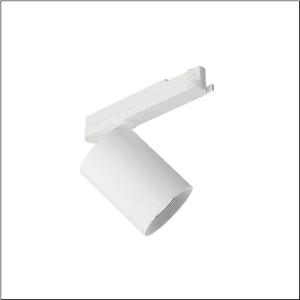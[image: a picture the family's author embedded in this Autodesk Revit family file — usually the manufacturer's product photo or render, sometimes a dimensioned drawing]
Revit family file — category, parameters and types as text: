
# Revit family: spot_21_51se12mbb5b
name_source: partatom
category: Lighting Fixtures
units: mm (PartAtom-declared; Revit-internal decimal feet)

## family parameters
Cut with Voids When Loaded = No
Host = Face
Light Source = No
Part Type = Normal
Room Calculation Point = No
Round Connector Dimension = Use Diameter
Shared = No

## types (1)
- --- (1 x LED, 5300 lm, 41.7 W, 3000K)
    Apparent Load = 42 VA
    CIE Flux Codes = 95 98 99 100 100
    Color Rendering = 90
    Color Temperature = 3000K
    Default Elevation = 1800 mm
    Description = Spot 21, directional spotlight, light control with lens, of PMMA, LED rated luminous flux: 5.100lm, light colour: 930, control gear: ECG Multilumen, with 3-phase adapter, mains connection: 220..240V, AC, 50/60Hz, of aluminium, traffic white (RAL 9016), length: 213mm, diameter: 105mm, protection rating (complete): IP20, insulation class (complete): insulation class I (protective earthing), certification: CE, impact resistance: IK02, permissible ambient temperature for indoor applications: -20..+40°C, packaging unit: 1 piece
    Height = 175 mm
    Lamp = 1 x LED
    Lamp Light Flux = 5300 lm
    Lamp Power = 41.7 W
    Lamp count = 1
    Length = 105 mm
    Luminous efficacy = 127 lm/W
    Manufacturer = Siteco
    ModVariant = No
    Model = 51SE12MBB5B
    Mounting Place = Ceiling
    Mounting Type = Pendant
    Number of Poles = 1
    OnlyDefault = Yes
    Power Factor = 1
    Product Name = Spot 21
    Product group = directional spotlight
    ProductGroupID = 905
    Protection Class = Protection class I
    Protection Degree = IP 20
    RLX_Detail_Level = 1
    RLX_Emergency_Light_Flux = 0 lm
    RLX_Emergency_Type = 0
    RLX_Emergency_Type_DB = No
    RlxData = <blob elided: 17649 chars, md5=ee2d00f4>
    Socket = socket
    Standby Power = 0 W
    System Light Flux = 5300 lm
    System Power = 42 W
    Type Comments = factory setting: luminous flux: 100 % | (ON | ON | ON | ON) | 1050 mA
    Type Image = l_1003976.jpg
    URL = http://relux.com
    VarID = @adj_114243
    Voltage = 0 V
    Weight = 0.00 kg
    Width = 0 mm  [stored 0 ft]

note: [stored X ft] marks values corroborated as IEEE doubles in the binary element streams (Revit-internal decimal feet)

## geometry (parser evidence)
native form markers: Blend x4, Sweep x10
no freeform markers — native parametric forms only
